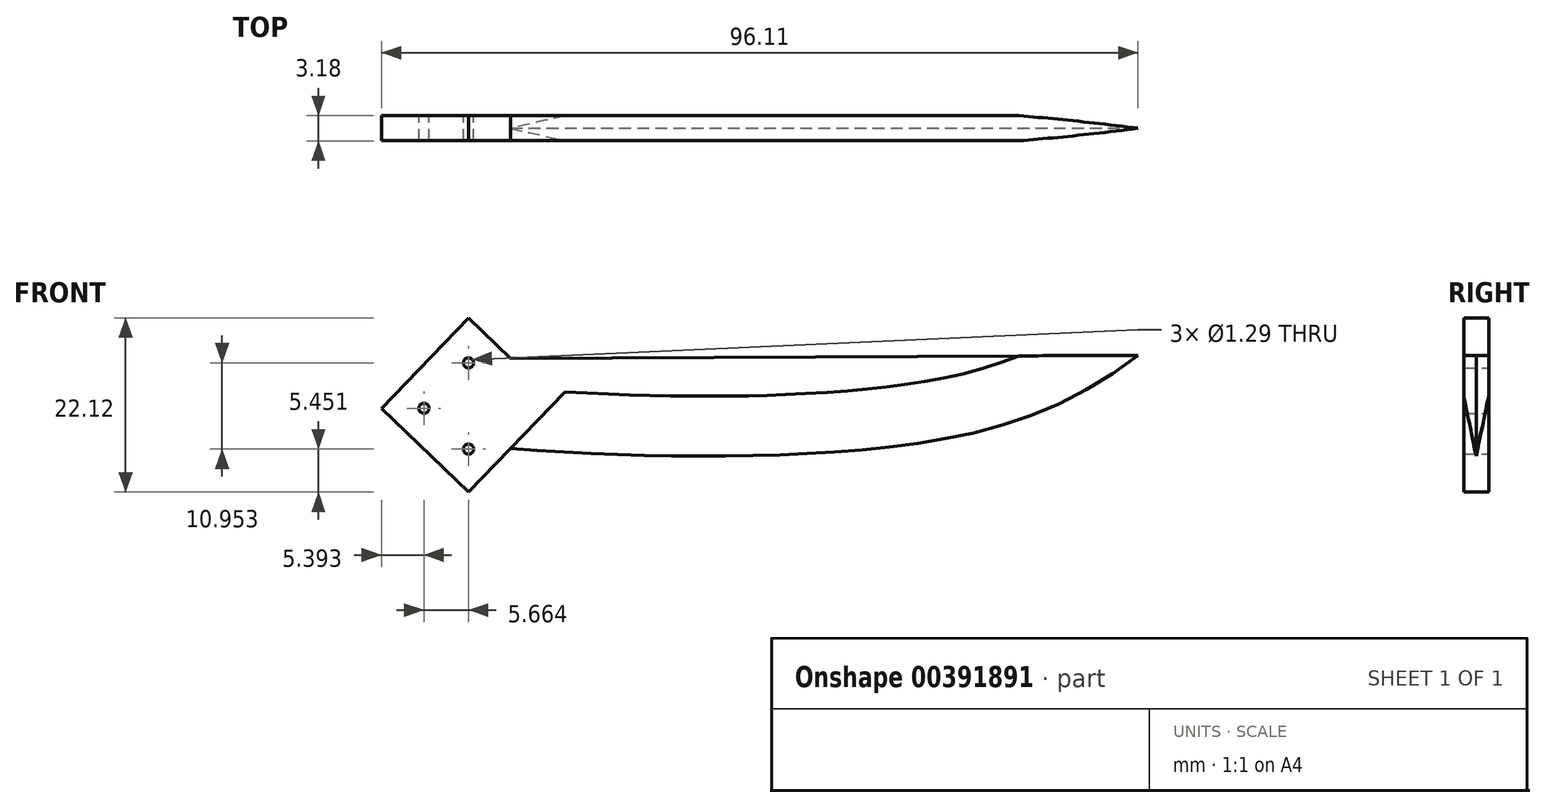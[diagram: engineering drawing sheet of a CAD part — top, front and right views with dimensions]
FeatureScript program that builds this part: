
annotation { "Feature Type Name" : "Feature", "Feature Type Description" : "" }
export const myFeature = defineFeature(function(context is Context, id is Id, definition is map)
    precondition{}
    {
        {
            var Q0;
            Q0=qCreatedBy(makeId("Front.planeOp"),FACE);
            var sketch = newSketch(context, id + "F0", { "sketchPlane" : qUnion([Q0])});
            skLineSegment(sketch, "E0", {"start": v(-39.5, 19.68) * mm, "end": v(-34, 25.4) * mm});
            skLineSegment(sketch, "E1", {"start": v(-34, 25.4) * mm, "end": v(-28.65, 20.26) * mm});
            skLineSegment(sketch, "E2", {"start": v(-39.66, 8.73) * mm, "end": v(-34, 3.28) * mm});
            skLineSegment(sketch, "E3", {"start": v(-34, 3.28) * mm, "end": v(-28.65, 8.83) * mm});
            skCircle(sketch, "E4", {"center": v(-34, 19.68) * mm, "radius": 0.64 * mm});
            skCircle(sketch, "E5", {"center": v(-34, 8.73) * mm, "radius": 0.64 * mm});
            skLineSegment(sketch, "E6", {"start": v(-39.5, 19.68) * mm, "end": v(-45.05, 13.92) * mm});
            skLineSegment(sketch, "E7", {"start": v(-39.66, 8.73) * mm, "end": v(-45.05, 13.92) * mm});
            skLineSegment(sketch, "E8", {"start": v(-28.65, 20.26) * mm, "end": v(51.06, 20.66) * mm});
            skFitSpline(sketch, "E9", {"points": [v(-28.65, 8.83) * mm, v(17.74, 8.83) * mm, v(51.06, 20.66) * mm], "startDerivative": vector(91, -6.78) * mm, "endDerivative": vector(66.13, 51.83) * mm});
            skCircle(sketch, "E10", {"center": v(-39.66, 13.92) * mm, "radius": 0.65 * mm});
            skSolve(sketch);
        }
        {
            var Q0;
            Q0=makeQuery(id+"F0.imprint","IMPRINT",FACE,{"disambiguationData":[TD([[makeQuery(id+"F0.imprint","IMPRINT",EDGE,{"derivedFrom":sQuery(id+"F0.wireOp",EDGE,"E0")}),-1.0]])]});
            extrude(context, id + "F1", {"entities" : qUnion([Q0]), "depth" : 3.17 * mm});
        }
        {
            var Q0;
            Q0=makeQuery(id+"F1.opExtrude","CAP_EDGE",EDGE,{"disambiguationData":[OSD([sQuery(id+"F0.wireOp",EDGE,"00c3c85d-c45e-48a6-aed7-b82995e2ba4a")])],"isStart":true});
            var Q1;
            Q1=makeQuery(id+"F1.opExtrude","CAP_EDGE",EDGE,{"disambiguationData":[OSD([sQuery(id+"F0.wireOp",EDGE,"00c3c85d-c45e-48a6-aed7-b82995e2ba4a")])],"isStart":false});
            var Q2;
            Q2=makeQuery(id+"F1.opExtrude","CAP_EDGE",EDGE,{"disambiguationData":[OSD([sQuery(id+"F0.wireOp",EDGE,"E9")])],"isStart":false});
            var Q3;
            Q3=makeQuery(id+"F1.opExtrude","CAP_EDGE",EDGE,{"disambiguationData":[OSD([sQuery(id+"F0.wireOp",EDGE,"E9")])],"isStart":true});
            chamfer(context, id + "F2", {"entities" : qUnion([Q0, Q1, Q2, Q3]), "chamferType" : ChamferType.TWO_OFFSETS, "width1" : 7.62 * mm, "oppositeDirection" : false, "width2" : 1.59 * mm, "tangentPropagation" : true});
        }
    });
